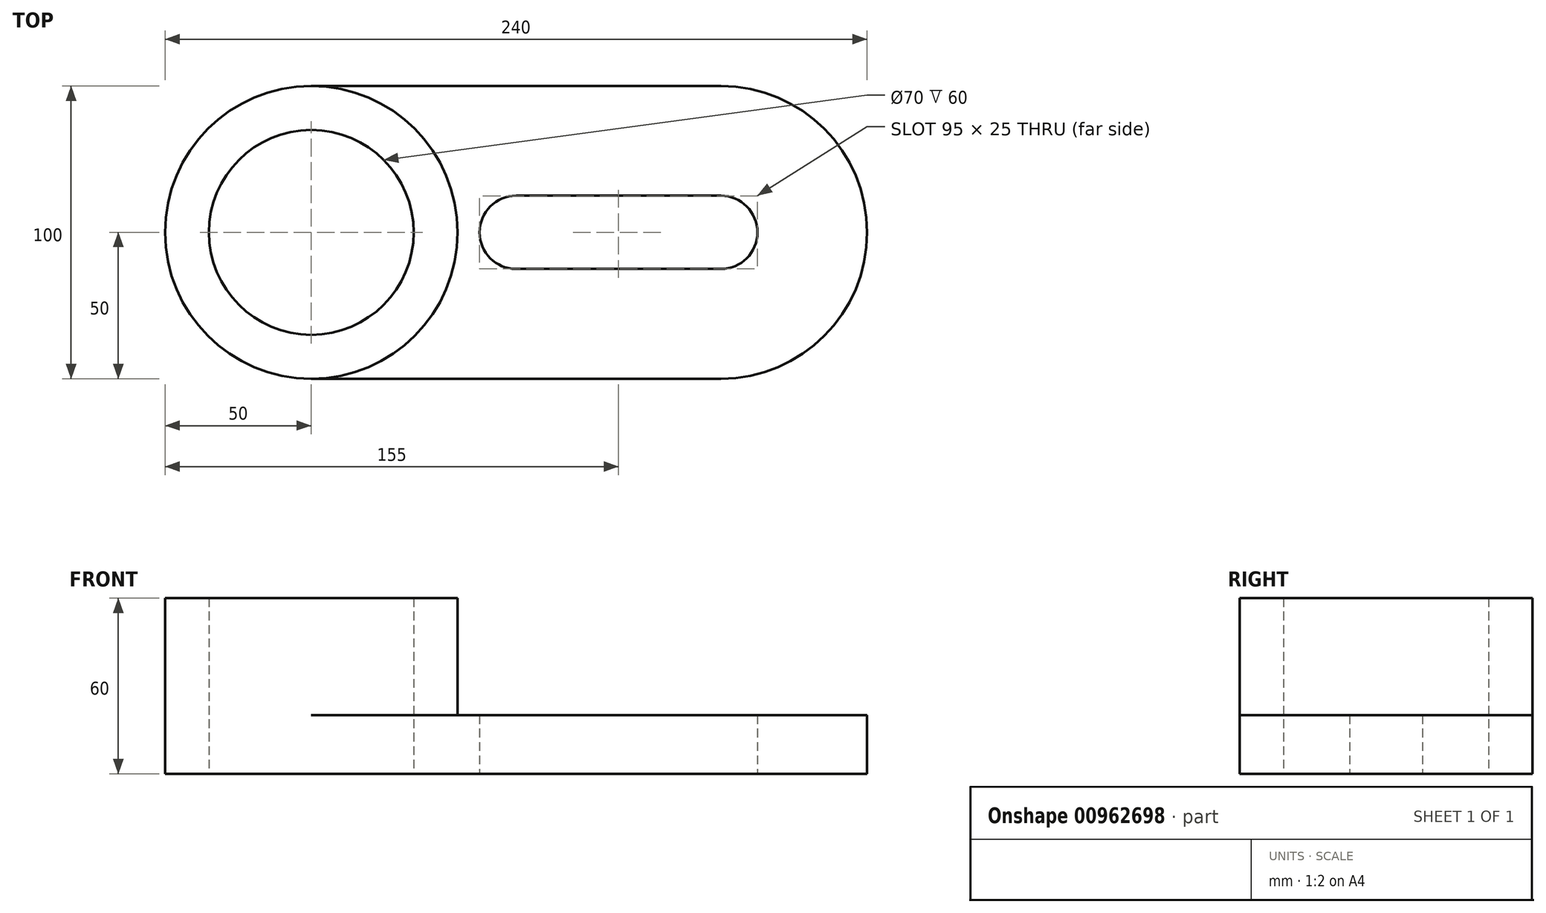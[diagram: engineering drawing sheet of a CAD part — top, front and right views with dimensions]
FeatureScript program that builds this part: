
annotation { "Feature Type Name" : "Feature", "Feature Type Description" : "" }
export const myFeature = defineFeature(function(context is Context, id is Id, definition is map)
    precondition{}
    {
        {
            var Q0;
            Q0=qCreatedBy(makeId("Top.planeOp"),FACE);
            var sketch = newSketch(context, id + "F0", { "sketchPlane" : qUnion([Q0])});
            skCircle(sketch, "E0", {"center": v(0, 0) * mm, "radius": 50 * mm});
            skCircle(sketch, "E1", {"center": v(0, 0) * mm, "radius": 35 * mm});
            skArc(sketch, "E2", {"start": v(140, -50) * mm, "mid": v(190, 0) * mm, "end": v(140, 50) * mm});
            skLineSegment(sketch, "E3", {"start": v(0, 50) * mm, "end": v(140, 50) * mm});
            skLineSegment(sketch, "E4", {"start": v(0, -50) * mm, "end": v(140, -50) * mm});
            skLineSegment(sketch, "E5", {"start": v(140, 0) * mm, "end": v(70, 0) * mm, "construction": true});
            skArc(sketch, "E6.0.startCap", {"start": v(140, 12.5) * mm, "mid": v(152.5, 0) * mm, "end": v(140, -12.5) * mm});
            skArc(sketch, "E6.0.endCap", {"start": v(70, -12.5) * mm, "mid": v(57.5, 0) * mm, "end": v(70, 12.5) * mm});
            skLineSegment(sketch, "E6.0.left", {"start": v(140, -12.5) * mm, "end": v(70, -12.5) * mm});
            skLineSegment(sketch, "E6.0.right", {"start": v(140, 12.5) * mm, "end": v(70, 12.5) * mm});
            skSolve(sketch);
        }
        {
            var Q0;
            Q0=makeQuery(id+"F0.imprint","IMPRINT",FACE,{"disambiguationData":[TD([[makeQuery(id+"F0.imprint","IMPRINT",EDGE,{"derivedFrom":sQuery(id+"F0.wireOp",EDGE,"E2")}),1.0]])]});
            var Q1;
            Q1=makeQuery(id+"F0.imprint","IMPRINT",FACE,{"disambiguationData":[TD([[makeQuery(id+"F0.imprint","IMPRINT",EDGE,{"derivedFrom":sQuery(id+"F0.wireOp",EDGE,"E1")}),-1.0]])]});
            extrude(context, id + "F1", {"entities" : qUnion([Q0, Q1]), "depth" : 20 * mm, "offsetDistance" : 25 * mm});
        }
        {
            var Q0;
            Q0=makeQuery(id+"F0.imprint","IMPRINT",FACE,{"disambiguationData":[TD([[makeQuery(id+"F0.imprint","IMPRINT",EDGE,{"derivedFrom":sQuery(id+"F0.wireOp",EDGE,"E1")}),-1.0]])]});
            extrude(context, id + "F2", {"entities" : qUnion([Q0]), "operationType" : NewBodyOperationType.ADD, "depth" : 60 * mm, "offsetDistance" : 25 * mm});
        }
    });
